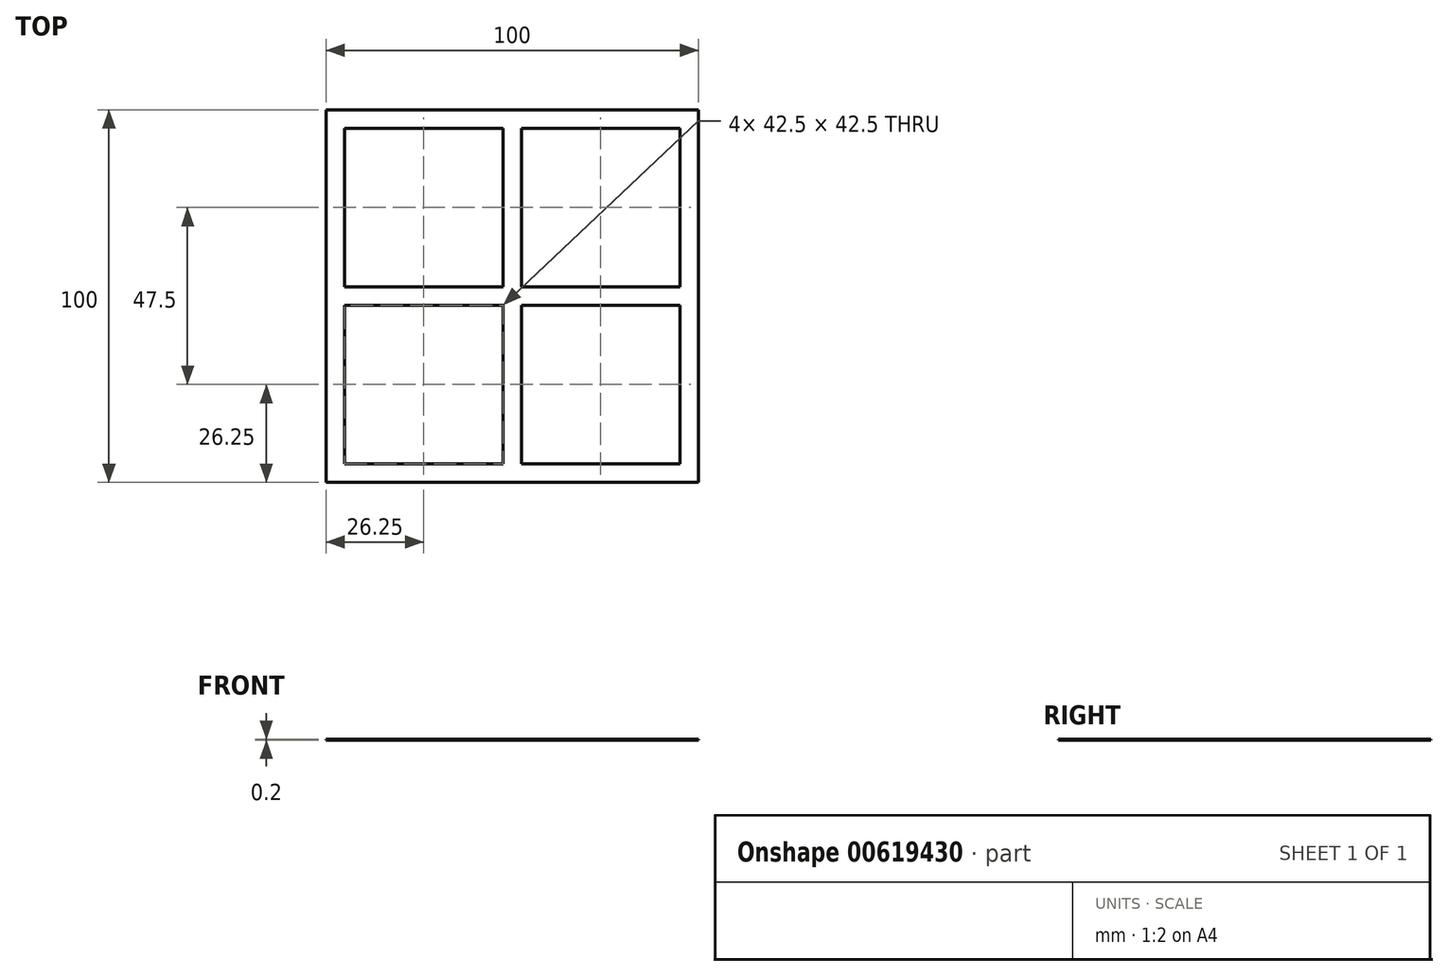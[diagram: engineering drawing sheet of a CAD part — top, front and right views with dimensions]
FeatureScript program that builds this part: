
annotation { "Feature Type Name" : "Feature", "Feature Type Description" : "" }
export const myFeature = defineFeature(function(context is Context, id is Id, definition is map)
    precondition{}
    {
        {
            var Q0;
            Q0=qCreatedBy(makeId("Top.planeOp"),FACE);
            var sketch = newSketch(context, id + "F0", { "sketchPlane" : qUnion([Q0])});
            skLineSegment(sketch, "E0.bottom", {"start": v(50, 50) * mm, "end": v(-50, 50) * mm});
            skLineSegment(sketch, "E0.top", {"start": v(50, -50) * mm, "end": v(-50, -50) * mm});
            skLineSegment(sketch, "E0.left", {"start": v(50, 50) * mm, "end": v(50, -50) * mm});
            skLineSegment(sketch, "E0.right", {"start": v(-50, 50) * mm, "end": v(-50, -50) * mm});
            skPoint(sketch, "E0.middle", {"position": v(0, 0) * mm});
            skLineSegment(sketch, "E1.0", {"start": v(45, 45) * mm, "end": v(45, 2.5) * mm});
            skLineSegment(sketch, "E1.1", {"start": v(45, 45) * mm, "end": v(2.5, 45) * mm});
            skLineSegment(sketch, "E1.2", {"start": v(-45, 45) * mm, "end": v(-45, 2.5) * mm});
            skLineSegment(sketch, "E1.3", {"start": v(45, -45) * mm, "end": v(2.5, -45) * mm});
            skLineSegment(sketch, "E2", {"start": v(-45, 2.5) * mm, "end": v(-2.5, 2.5) * mm});
            skLineSegment(sketch, "E3.MirrorCS", {"start": v(-45, -2.5) * mm, "end": v(-2.5, -2.5) * mm});
            skLineSegment(sketch, "E4", {"start": v(-2.5, 45) * mm, "end": v(-2.5, 2.5) * mm});
            skLineSegment(sketch, "E5.MirrorCS", {"start": v(2.5, 45) * mm, "end": v(2.5, 2.5) * mm});
            skLineSegment(sketch, "E6.trimOffspring", {"start": v(-2.5, -2.5) * mm, "end": v(-2.5, -45) * mm});
            skLineSegment(sketch, "E7.trimOffspring", {"start": v(2.5, 2.5) * mm, "end": v(45, 2.5) * mm});
            skLineSegment(sketch, "E8.trimOffspring", {"start": v(2.5, -2.5) * mm, "end": v(2.5, -45) * mm});
            skLineSegment(sketch, "E9.trimOffspring", {"start": v(2.5, -2.5) * mm, "end": v(45, -2.5) * mm});
            skLineSegment(sketch, "E10.trimOffspring", {"start": v(-2.5, -45) * mm, "end": v(-45, -45) * mm});
            skLineSegment(sketch, "E11.trimOffspring", {"start": v(-45, -2.5) * mm, "end": v(-45, -45) * mm});
            skLineSegment(sketch, "E12.trimOffspring", {"start": v(45, -2.5) * mm, "end": v(45, -45) * mm});
            skLineSegment(sketch, "E13.trimOffspring", {"start": v(-2.5, 45) * mm, "end": v(-45, 45) * mm});
            skSolve(sketch);
        }
        {
            var Q0;
            Q0=makeQuery(id+"F0.imprint","IMPRINT",FACE,{"disambiguationData":[TD([[makeQuery(id+"F0.imprint","IMPRINT",EDGE,{"derivedFrom":sQuery(id+"F0.wireOp",EDGE,"E0.bottom")}),1.0]])]});
            extrude(context, id + "F1", {"entities" : qUnion([Q0]), "depth" : 0.2 * mm, "offsetDistance" : 25 * mm});
        }
    });
